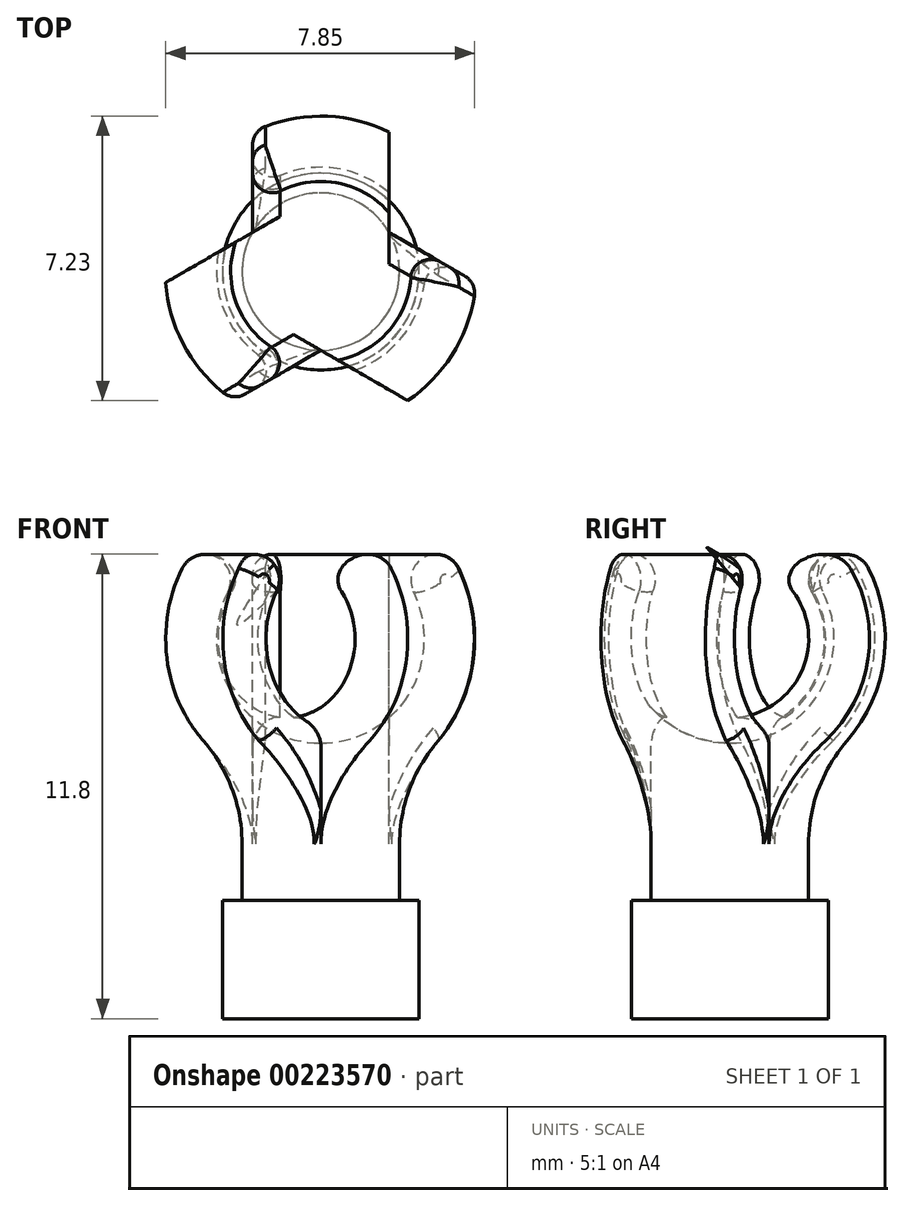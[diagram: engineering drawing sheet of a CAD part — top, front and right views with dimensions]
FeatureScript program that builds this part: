
annotation { "Feature Type Name" : "Feature", "Feature Type Description" : "" }
export const myFeature = defineFeature(function(context is Context, id is Id, definition is map)
    precondition{}
    {
        {
            var Q0;
            Q0=qCreatedBy(makeId("Right.planeOp"),FACE);
            var sketch = newSketch(context, id + "F0", { "sketchPlane" : qUnion([Q0])});
            skArc(sketch, "E0", {"start": v(-3.52, 1.8) * mm, "mid": v(-3.37, -2.06) * mm, "end": v(0, -3.95) * mm});
            skArc(sketch, "E1", {"start": v(-2.36, 1.2) * mm, "mid": v(-2.26, -1.38) * mm, "end": v(0, -2.65) * mm});
            skLineSegment(sketch, "E2", {"start": v(0, -2.65) * mm, "end": v(0, -3.95) * mm});
            skLineSegment(sketch, "E3", {"start": v(0, 0) * mm, "end": v(-3.52, 1.8) * mm, "construction": true});
            skPoint(sketch, "E4.end.orphan", {"position": v(0, 2.65) * mm});
            skPoint(sketch, "E4.start.orphan", {"position": v(0, 3.95) * mm});
            skArc(sketch, "E5", {"start": v(-2.36, 1.2) * mm, "mid": v(-2.65, 2.08) * mm, "end": v(-3.52, 1.8) * mm});
            skCircle(sketch, "E6", {"center": v(0, 0) * mm, "radius": 2.5 * mm, "construction": true});
            skLineSegment(sketch, "E7", {"start": v(-2.5, 0) * mm, "end": v(-2.5, 2.5) * mm, "construction": true});
            skLineSegment(sketch, "E8", {"start": v(0, 2.5) * mm, "end": v(-2.5, 2.5) * mm, "construction": true});
            skSolve(sketch);
        }
        {
            var Q0;
            Q0=makeQuery(id+"F0.imprint","IMPRINT",FACE,{"disambiguationData":[TD([[makeQuery(id+"F0.imprint","IMPRINT",EDGE,{"derivedFrom":sQuery(id+"F0.wireOp",EDGE,"E0")}),1.0]])]});
            var Q1;
            Q1=sQuery(id+"F0.wireOp",EDGE,"E2");
            revolve(context, id + "F1", {"entities" : qUnion([Q0]), "axis" : qUnion([Q1]), "revolveType" : RevolveType.FULL});
        }
        {
            var Q0;
            Q0=qCreatedBy(makeId("Top.planeOp"),FACE);
            var sketch = newSketch(context, id + "F2", { "sketchPlane" : qUnion([Q0])});
            skLineSegment(sketch, "E9", {"start": v(0, 0) * mm, "end": v(19.8, 11.43) * mm, "construction": true});
            skLineSegment(sketch, "E10", {"start": v(1.73, 1) * mm, "end": v(1.73, 9.08) * mm});
            skLineSegment(sketch, "E11", {"start": v(1.73, 9.08) * mm, "end": v(5.23, 3.02) * mm});
            skLineSegment(sketch, "E12.MirrorCS", {"start": v(1.73, 1) * mm, "end": v(8.73, -3.04) * mm});
            skLineSegment(sketch, "E13.MirrorCS", {"start": v(8.73, -3.04) * mm, "end": v(5.23, 3.02) * mm});
            skLineSegment(sketch, "E14.1.0", {"start": v(-1.73, 1) * mm, "end": v(-1.73, 9.08) * mm});
            skLineSegment(sketch, "E14.1.1", {"start": v(-1.73, 1) * mm, "end": v(-8.73, -3.04) * mm});
            skLineSegment(sketch, "E14.1.2", {"start": v(-8.73, -3.04) * mm, "end": v(-5.23, 3.02) * mm});
            skLineSegment(sketch, "E14.1.3", {"start": v(-1.73, 9.08) * mm, "end": v(-5.23, 3.02) * mm});
            skLineSegment(sketch, "E14.2.0", {"start": v(0, -2) * mm, "end": v(-7, -6.04) * mm});
            skLineSegment(sketch, "E14.2.1", {"start": v(0, -2) * mm, "end": v(7, -6.04) * mm});
            skLineSegment(sketch, "E14.2.2", {"start": v(7, -6.04) * mm, "end": v(0, -6.04) * mm});
            skLineSegment(sketch, "E14.2.3", {"start": v(-7, -6.04) * mm, "end": v(0, -6.04) * mm});
            skPoint(sketch, "E14.center", {"position": v(0, 0) * mm});
            skSolve(sketch);
        }
        {
            var Q0;
            Q0=qSketchRegion(id+"F2",true);
            extrude(context, id + "F3", {"entities" : qUnion([Q0]), "operationType" : NewBodyOperationType.REMOVE, "oppositeDirection" : true, "depth" : 25 * mm, "hasSecondDirection" : true, "secondDirectionOppositeDirection" : false, "secondDirectionDepth" : 25 * mm});
        }
        {
            var Q0;
            Q0=qCreatedBy(makeId("Front.planeOp"),FACE);
            var sketch = newSketch(context, id + "F4", { "sketchPlane" : qUnion([Q0])});
            skLineSegment(sketch, "E15.bottom", {"start": v(0, -2.65) * mm, "end": v(2, -2.65) * mm});
            skLineSegment(sketch, "E15.top", {"start": v(0, -6.65) * mm, "end": v(2, -6.65) * mm});
            skLineSegment(sketch, "E15.left", {"start": v(0, -2.65) * mm, "end": v(0, -6.65) * mm});
            skLineSegment(sketch, "E15.right", {"start": v(2, -2.65) * mm, "end": v(2, -6.65) * mm});
            skSolve(sketch);
        }
        {
            var Q0;
            Q0=qSketchRegion(id+"F4",true);
            var Q1;
            Q1=sQuery(id+"F4.wireOp",EDGE,"E15.left");
            revolve(context, id + "F5", {"operationType" : NewBodyOperationType.ADD, "entities" : qUnion([Q0]), "axis" : qUnion([Q1]), "revolveType" : RevolveType.FULL});
        }
        {
            var Q0;
            Q0=makeQuery(id+"F5.boolean.opBoolean","INTERSECT",EDGE,{"disambiguationData":[OD(2.0)],"derivedFrom":[makeQuery(id+"F1.opRevolve","SWEPT_FACE",FACE,{"disambiguationData":[OSD([sQuery(id+"F0.wireOp",EDGE,"E0")])]}),makeQuery(id+"F5.opRevolve","SWEPT_FACE",FACE,{"disambiguationData":[OSD([sQuery(id+"F4.wireOp",EDGE,"E15.right")])]})]});
            var Q1;
            Q1=makeQuery(id+"F5.boolean.opBoolean","INTERSECT",EDGE,{"disambiguationData":[OD(1.0)],"derivedFrom":[makeQuery(id+"F1.opRevolve","SWEPT_FACE",FACE,{"disambiguationData":[OSD([sQuery(id+"F0.wireOp",EDGE,"E0")])]}),makeQuery(id+"F5.opRevolve","SWEPT_FACE",FACE,{"disambiguationData":[OSD([sQuery(id+"F4.wireOp",EDGE,"E15.right")])]})]});
            var Q2;
            Q2=makeQuery(id+"F5.boolean.opBoolean","INTERSECT",EDGE,{"disambiguationData":[OD(0.0)],"derivedFrom":[makeQuery(id+"F1.opRevolve","SWEPT_FACE",FACE,{"disambiguationData":[OSD([sQuery(id+"F0.wireOp",EDGE,"E0")])]}),makeQuery(id+"F5.opRevolve","SWEPT_FACE",FACE,{"disambiguationData":[OSD([sQuery(id+"F4.wireOp",EDGE,"E15.right")])]})]});
            fillet(context, id + "F6", {"entities" : qUnion([Q0, Q1, Q2]), "radius" : 4 * mm, "tangentPropagation" : true, "allowEdgeOverflow" : false});
        }
        {
            var Q0;
            Q0=makeQuery(id+"F5.opRevolve","SWEPT_FACE",FACE,{"disambiguationData":[OSD([sQuery(id+"F4.wireOp",EDGE,"E15.top")])]});
            var sketch = newSketch(context, id + "F7", { "sketchPlane" : qUnion([Q0])});
            skCircle(sketch, "E16", {"center": v(0, 0) * mm, "radius": 2.5 * mm});
            skSolve(sketch);
        }
        {
            var Q0;
            Q0=qSketchRegion(id+"F7",true);
            extrude(context, id + "F8", {"entities" : qUnion([Q0]), "operationType" : NewBodyOperationType.ADD, "depth" : 3 * mm});
        }
        {
            var Q0;
            Q0=qCreatedBy(makeId("Top.planeOp"),FACE);
            var sketch = newSketch(context, id + "F9", { "sketchPlane" : qUnion([Q0])});
            skCircle(sketch, "E17.cCircle", {"center": v(0, 0) * mm, "radius": 2.15 * mm, "construction": true});
            skLineSegment(sketch, "E17.0", {"start": v(-1.56, 2.15) * mm, "end": v(1.56, 2.15) * mm});
            skLineSegment(sketch, "E17.1", {"start": v(1.56, 2.15) * mm, "end": v(2.53, -0.82) * mm});
            skLineSegment(sketch, "E17.2", {"start": v(2.53, -0.82) * mm, "end": v(0, -2.66) * mm});
            skLineSegment(sketch, "E17.3", {"start": v(0, -2.66) * mm, "end": v(-2.53, -0.82) * mm});
            skLineSegment(sketch, "E17.4", {"start": v(-2.53, -0.82) * mm, "end": v(-1.56, 2.15) * mm});
            skPoint(sketch, "E17.0.midPoint", {"position": v(0, 2.15) * mm});
            skSolve(sketch);
        }
        {
            var Q0;
            Q0=makeQuery(id+"F3.boolean.opBoolean","INTERSECT",EDGE,{"derivedFrom":[makeQuery(id+"F1.opRevolve","SWEPT_FACE",FACE,{"disambiguationData":[OSD([sQuery(id+"F0.wireOp",EDGE,"E5")])]}),makeQuery(id+"F3.opExtrude","SWEPT_FACE",FACE,{"disambiguationData":[OSD([sQuery(id+"F2.wireOp",EDGE,"E14.2.0")])]})]});
            var Q1;
            Q1=makeQuery(id+"F3.boolean.opBoolean","INTERSECT",EDGE,{"derivedFrom":[makeQuery(id+"F1.opRevolve","SWEPT_FACE",FACE,{"disambiguationData":[OSD([sQuery(id+"F0.wireOp",EDGE,"E5")])]}),makeQuery(id+"F3.opExtrude","SWEPT_FACE",FACE,{"disambiguationData":[OSD([sQuery(id+"F2.wireOp",EDGE,"E14.1.0")])]})]});
            var Q2;
            Q2=makeQuery(id+"F3.boolean.opBoolean","INTERSECT",EDGE,{"derivedFrom":[makeQuery(id+"F1.opRevolve","SWEPT_FACE",FACE,{"disambiguationData":[OSD([sQuery(id+"F0.wireOp",EDGE,"E5")])]}),makeQuery(id+"F3.opExtrude","SWEPT_FACE",FACE,{"disambiguationData":[OSD([sQuery(id+"F2.wireOp",EDGE,"E12.MirrorCS")])]})]});
            fillet(context, id + "F10", {"entities" : qUnion([Q0, Q1, Q2]), "radius" : 0.5 * mm, "tangentPropagation" : true, "allowEdgeOverflow" : false});
        }
    });
